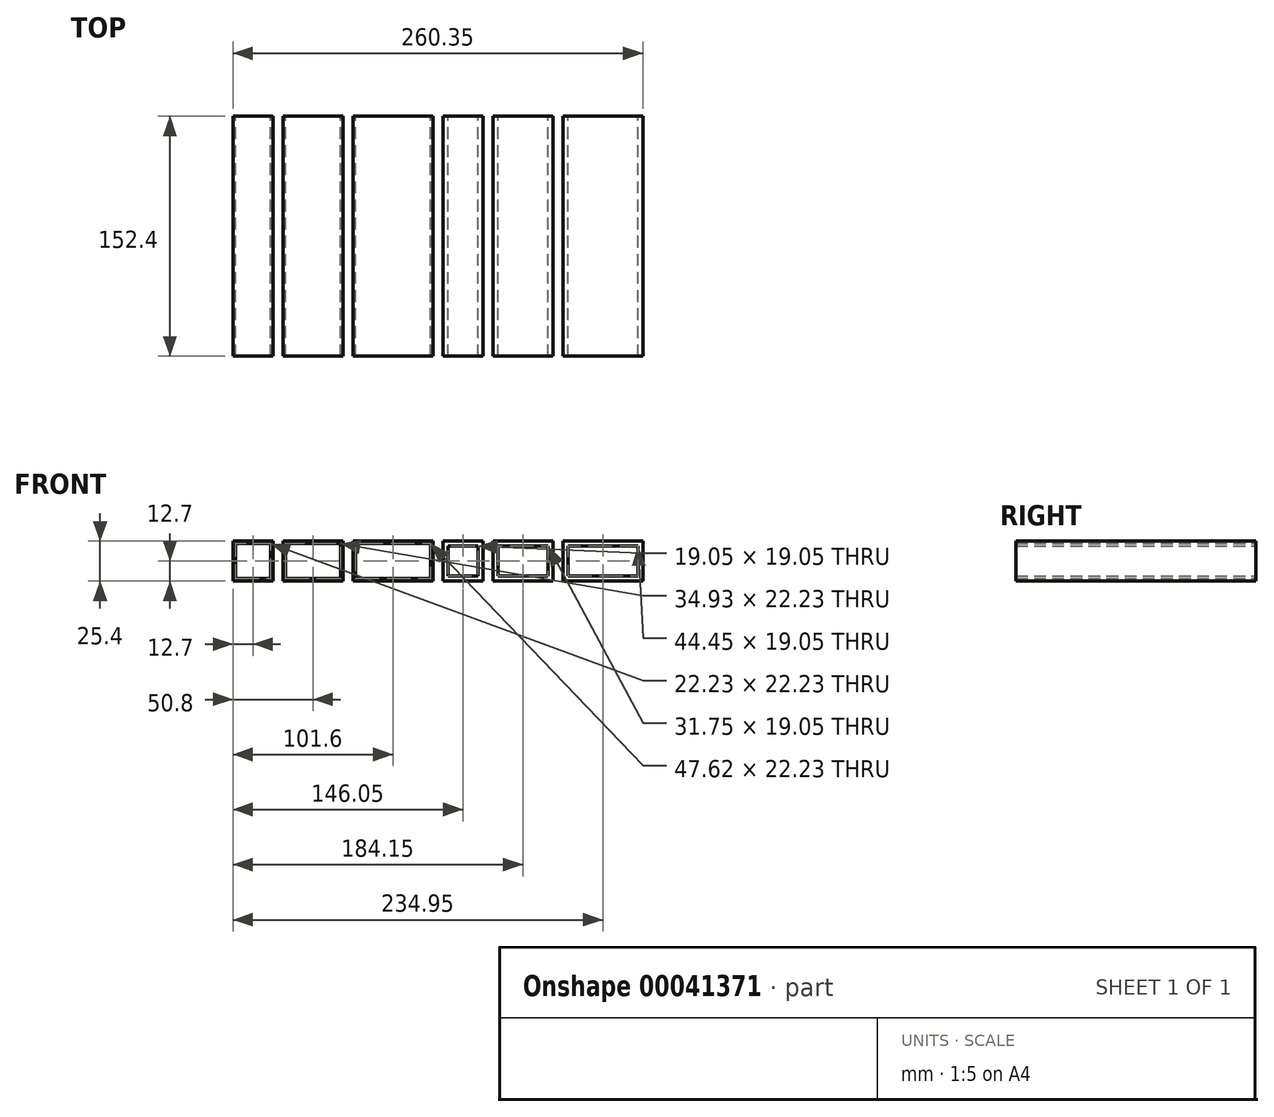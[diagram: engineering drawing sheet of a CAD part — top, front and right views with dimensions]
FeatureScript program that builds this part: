
annotation { "Feature Type Name" : "Feature", "Feature Type Description" : "" }
export const myFeature = defineFeature(function(context is Context, id is Id, definition is map)
    precondition{}
    {
        {
            var Q0;
            Q0=qCreatedBy(makeId("Front.planeOp"),FACE);
            var sketch = newSketch(context, id + "F0", { "sketchPlane" : qUnion([Q0])});
            skLineSegment(sketch, "E0", {"start": v(0, 0) * mm, "end": v(310.95, 0) * mm, "construction": true});
            skLineSegment(sketch, "E1", {"start": v(0, 12.7) * mm, "end": v(304.33, 12.7) * mm, "construction": true});
            skLineSegment(sketch, "E2.rect.bottom", {"start": v(0, 0) * mm, "end": v(25.4, 0) * mm});
            skLineSegment(sketch, "E2.rect.top", {"start": v(0, 25.4) * mm, "end": v(25.4, 25.4) * mm});
            skLineSegment(sketch, "E2.rect.left", {"start": v(0, 0) * mm, "end": v(0, 25.4) * mm});
            skLineSegment(sketch, "E2.rect.right", {"start": v(25.4, 0) * mm, "end": v(25.4, 25.4) * mm});
            skPoint(sketch, "E2.rect.middle", {"position": v(12.7, 12.7) * mm});
            skLineSegment(sketch, "E3.rect.bottom", {"start": v(1.59, 23.81) * mm, "end": v(23.81, 23.81) * mm});
            skLineSegment(sketch, "E3.rect.top", {"start": v(1.59, 1.59) * mm, "end": v(23.81, 1.59) * mm});
            skLineSegment(sketch, "E3.rect.left", {"start": v(1.59, 23.81) * mm, "end": v(1.59, 1.59) * mm});
            skLineSegment(sketch, "E3.rect.right", {"start": v(23.81, 23.81) * mm, "end": v(23.81, 1.59) * mm});
            skLineSegment(sketch, "E4.rect.bottom", {"start": v(33.34, 23.81) * mm, "end": v(68.26, 23.81) * mm});
            skLineSegment(sketch, "E4.rect.top", {"start": v(33.34, 1.59) * mm, "end": v(68.26, 1.59) * mm});
            skLineSegment(sketch, "E4.rect.left", {"start": v(33.34, 23.81) * mm, "end": v(33.34, 1.59) * mm});
            skLineSegment(sketch, "E4.rect.right", {"start": v(68.26, 23.81) * mm, "end": v(68.26, 1.59) * mm});
            skPoint(sketch, "E4.rect.middle", {"position": v(50.8, 12.7) * mm});
            skLineSegment(sketch, "E5.rect.bottom", {"start": v(31.75, 0) * mm, "end": v(69.85, 0) * mm});
            skLineSegment(sketch, "E5.rect.top", {"start": v(31.75, 25.4) * mm, "end": v(69.85, 25.4) * mm});
            skLineSegment(sketch, "E5.rect.left", {"start": v(31.75, 0) * mm, "end": v(31.75, 25.4) * mm});
            skLineSegment(sketch, "E5.rect.right", {"start": v(69.85, 0) * mm, "end": v(69.85, 25.4) * mm});
            skLineSegment(sketch, "E6.rect.bottom", {"start": v(77.79, 1.59) * mm, "end": v(125.41, 1.59) * mm});
            skLineSegment(sketch, "E6.rect.top", {"start": v(77.79, 23.81) * mm, "end": v(125.41, 23.81) * mm});
            skLineSegment(sketch, "E6.rect.left", {"start": v(77.79, 1.59) * mm, "end": v(77.79, 23.81) * mm});
            skLineSegment(sketch, "E6.rect.right", {"start": v(125.41, 1.59) * mm, "end": v(125.41, 23.81) * mm});
            skPoint(sketch, "E6.rect.middle", {"position": v(101.6, 12.7) * mm});
            skLineSegment(sketch, "E7.rect.bottom", {"start": v(76.2, 0) * mm, "end": v(127, 0) * mm});
            skLineSegment(sketch, "E7.rect.top", {"start": v(76.2, 25.4) * mm, "end": v(127, 25.4) * mm});
            skLineSegment(sketch, "E7.rect.left", {"start": v(76.2, 0) * mm, "end": v(76.2, 25.4) * mm});
            skLineSegment(sketch, "E7.rect.right", {"start": v(127, 0) * mm, "end": v(127, 25.4) * mm});
            skLineSegment(sketch, "E8.rect.bottom", {"start": v(136.53, 3.18) * mm, "end": v(155.57, 3.18) * mm});
            skLineSegment(sketch, "E8.rect.top", {"start": v(136.53, 22.23) * mm, "end": v(155.57, 22.23) * mm});
            skLineSegment(sketch, "E8.rect.left", {"start": v(136.53, 3.18) * mm, "end": v(136.53, 22.23) * mm});
            skLineSegment(sketch, "E8.rect.right", {"start": v(155.57, 3.18) * mm, "end": v(155.57, 22.23) * mm});
            skPoint(sketch, "E8.rect.middle", {"position": v(146.05, 12.7) * mm});
            skLineSegment(sketch, "E9.rect.bottom", {"start": v(133.35, 0) * mm, "end": v(158.75, 0) * mm});
            skLineSegment(sketch, "E9.rect.top", {"start": v(133.35, 25.4) * mm, "end": v(158.75, 25.4) * mm});
            skLineSegment(sketch, "E9.rect.left", {"start": v(133.35, 0) * mm, "end": v(133.35, 25.4) * mm});
            skLineSegment(sketch, "E9.rect.right", {"start": v(158.75, 0) * mm, "end": v(158.75, 25.4) * mm});
            skLineSegment(sketch, "E10.rect.bottom", {"start": v(168.28, 22.22) * mm, "end": v(200.03, 22.22) * mm});
            skLineSegment(sketch, "E10.rect.top", {"start": v(168.28, 3.18) * mm, "end": v(200.03, 3.18) * mm});
            skLineSegment(sketch, "E10.rect.left", {"start": v(168.28, 22.22) * mm, "end": v(168.28, 3.18) * mm});
            skLineSegment(sketch, "E10.rect.right", {"start": v(200.03, 22.22) * mm, "end": v(200.03, 3.18) * mm});
            skPoint(sketch, "E10.rect.middle", {"position": v(184.15, 12.7) * mm});
            skLineSegment(sketch, "E11.rect.bottom", {"start": v(165.1, 0) * mm, "end": v(203.2, 0) * mm});
            skLineSegment(sketch, "E11.rect.top", {"start": v(165.1, 25.4) * mm, "end": v(203.2, 25.4) * mm});
            skLineSegment(sketch, "E11.rect.left", {"start": v(165.1, 0) * mm, "end": v(165.1, 25.4) * mm});
            skLineSegment(sketch, "E11.rect.right", {"start": v(203.2, 0) * mm, "end": v(203.2, 25.4) * mm});
            skLineSegment(sketch, "E12.rect.bottom", {"start": v(212.72, 3.18) * mm, "end": v(257.18, 3.18) * mm});
            skLineSegment(sketch, "E12.rect.top", {"start": v(212.72, 22.23) * mm, "end": v(257.18, 22.23) * mm});
            skLineSegment(sketch, "E12.rect.left", {"start": v(212.72, 3.18) * mm, "end": v(212.72, 22.22) * mm});
            skLineSegment(sketch, "E12.rect.right", {"start": v(257.18, 3.18) * mm, "end": v(257.18, 22.22) * mm});
            skPoint(sketch, "E12.rect.middle", {"position": v(234.95, 12.7) * mm});
            skLineSegment(sketch, "E13.rect.bottom", {"start": v(209.55, 0) * mm, "end": v(260.35, 0) * mm});
            skLineSegment(sketch, "E13.rect.top", {"start": v(209.55, 25.4) * mm, "end": v(260.35, 25.4) * mm});
            skLineSegment(sketch, "E13.rect.left", {"start": v(209.55, 0) * mm, "end": v(209.55, 25.4) * mm});
            skLineSegment(sketch, "E13.rect.right", {"start": v(260.35, 0) * mm, "end": v(260.35, 25.4) * mm});
            skSolve(sketch);
        }
        {
            var Q0;
            Q0=makeQuery(id+"F0.imprint","IMPRINT",FACE,{"disambiguationData":[TD([[makeQuery(id+"F0.imprint","IMPRINT",EDGE,{"derivedFrom":sQuery(id+"F0.wireOp",EDGE,"E2.rect.bottom")}),1.0]])]});
            var Q1;
            Q1=makeQuery(id+"F0.imprint","IMPRINT",FACE,{"disambiguationData":[TD([[makeQuery(id+"F0.imprint","IMPRINT",EDGE,{"derivedFrom":sQuery(id+"F0.wireOp",EDGE,"E4.rect.bottom")}),1.0]])]});
            var Q2;
            Q2=makeQuery(id+"F0.imprint","IMPRINT",FACE,{"disambiguationData":[TD([[makeQuery(id+"F0.imprint","IMPRINT",EDGE,{"derivedFrom":sQuery(id+"F0.wireOp",EDGE,"E6.rect.bottom")}),-1.0]])]});
            var Q3;
            Q3=makeQuery(id+"F0.imprint","IMPRINT",FACE,{"disambiguationData":[TD([[makeQuery(id+"F0.imprint","IMPRINT",EDGE,{"derivedFrom":sQuery(id+"F0.wireOp",EDGE,"E8.rect.bottom")}),-1.0]])]});
            var Q4;
            Q4=makeQuery(id+"F0.imprint","IMPRINT",FACE,{"disambiguationData":[TD([[makeQuery(id+"F0.imprint","IMPRINT",EDGE,{"derivedFrom":sQuery(id+"F0.wireOp",EDGE,"E10.rect.bottom")}),1.0]])]});
            var Q5;
            Q5=makeQuery(id+"F0.imprint","IMPRINT",FACE,{"disambiguationData":[TD([[makeQuery(id+"F0.imprint","IMPRINT",EDGE,{"derivedFrom":sQuery(id+"F0.wireOp",EDGE,"E12.rect.bottom")}),-1.0]])]});
            extrude(context, id + "F1", {"entities" : qUnion([Q0, Q1, Q2, Q3, Q4, Q5]), "depth" : 152.4 * mm});
        }
    });
